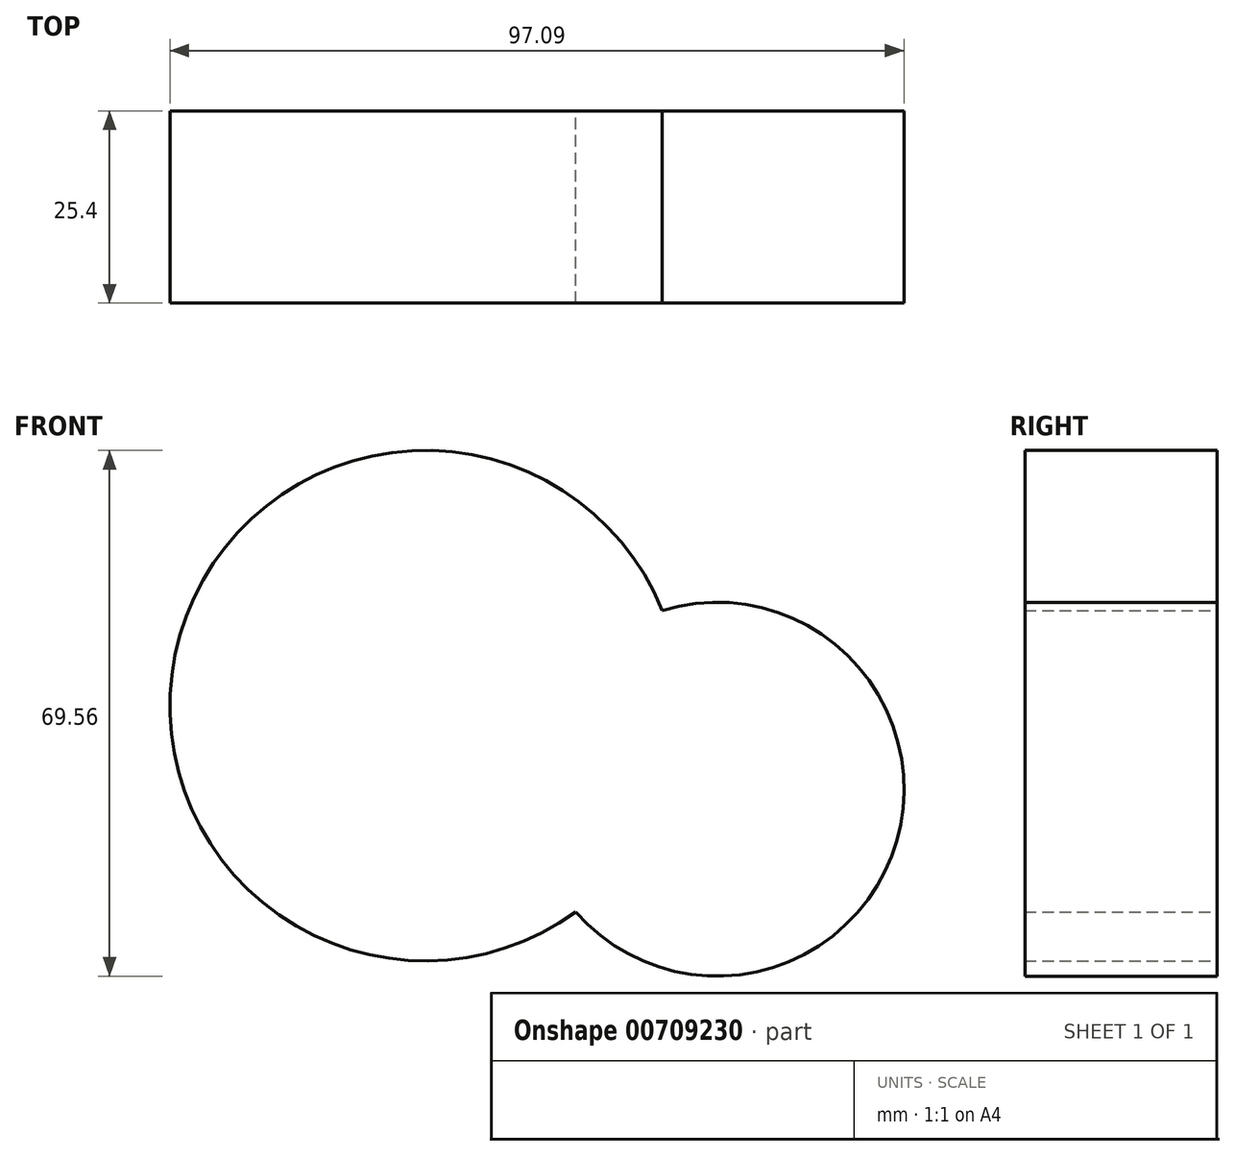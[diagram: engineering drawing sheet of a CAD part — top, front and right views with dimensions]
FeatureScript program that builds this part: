
annotation { "Feature Type Name" : "Feature", "Feature Type Description" : "" }
export const myFeature = defineFeature(function(context is Context, id is Id, definition is map)
    precondition{}
    {
        {
            var Q0;
            Q0=qCreatedBy(makeId("Front.planeOp"),FACE);
            var sketch = newSketch(context, id + "F0", { "sketchPlane" : qUnion([Q0])});
            skArc(sketch, "E0", {"start": v(-46.31, -46.58) * mm, "mid": v(4.4, -66.47) * mm, "end": v(55.71, -48.2) * mm});
            skArc(sketch, "E1", {"start": v(5.62, 11.27) * mm, "mid": v(48.08, 20.68) * mm, "end": v(17.05, 51.15) * mm});
            skArc(sketch, "E2", {"start": v(17.05, 51.15) * mm, "mid": v(-46.74, 47.85) * mm, "end": v(5.62, 11.27) * mm});
            skSolve(sketch);
        }
        {
            var Q0;
            Q0 = qSketchRegion(id + "F0", true);
            extrude(context, id + "F1", {"entities" : qUnion([Q0]), "depth" : 25.4 * mm, "offsetDistance" : 25.4 * mm});
        }
    });
